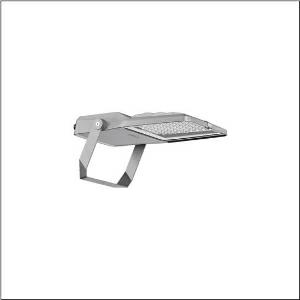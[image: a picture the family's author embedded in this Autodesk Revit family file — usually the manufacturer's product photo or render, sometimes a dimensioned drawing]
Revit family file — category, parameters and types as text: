
# Revit family: floodlight_fl_21_iq_mini___pl43_5xa7772c5a1a_be68
name_source: partatom
category: Lighting Fixtures
units: mm (PartAtom-declared; Revit-internal decimal feet)

## family parameters
Cut with Voids When Loaded = No
Host = Face
Light Source = No
Part Type = Normal
Room Calculation Point = No
Round Connector Dimension = Use Diameter
Shared = No

## types (1)
- --- (1 x LED, 11690 lm, 87.2 W, 4000K)
    Apparent Load = 87 VA
    CIE Flux Codes = 27 78 99 100 100
    Color Rendering = 80
    Color Temperature = 4000K
    Default Elevation = 1800 mm
    Description = Floodlight FL 21 iQ mini, floodlight, primary light control with lens, of PMMA, primary optical cover: protective disc, of toughened safety glass, transparent, light distribution: PL43, light emission: direct distribution, installation type: surface-mounted, lamps: LED, High Power LED, rated values: 11.690lm | 87,2W | 134,1lm/W (begin service life); end service life: 11.690lm | 92,1W; at 50% lumin. flux: 5.845lm | 40,1W | 145,8lm/W, colour temperature: 4000K, colour rendering: CRI > 80, light colour: 840, light setting 1 begin service life: 100% | 11.690lm | 87,2W | 134,1lm/W | 4.000K, light setting 1 end service life: 92,1W, further light settings possible, control: Street-Remote, Auto-Match, Temp-Guard, Night-Set, Smart-Wire, Desk-Remote (wireless, voltage-free reading and setting of iQ features in the workshop via application-optimized NFC function/RFID function), optimised constant luminous flux control (CLO 2.0), pre-setting: linear dimming characteristic, with terminal, 6-pole, mains connection: 220..240V, AC, 50/60Hz, luminaire housing, of diecast aluminium, powder-coated, SITECO metallic grey (DB 702S), corrosivity category C5 mid according to DIN EN ISO 12944suitable for swimming poolschlorine-resistant, sealing non-destructively replaceable, mounting bracket, of steel, galvanised, powder-coated, SITECO metallic grey (DB 702S), protection rating (complete): IP66, insulation class (complete): insulation class II (safety insulation), certification: CE, ENEC, VDE, protection symbol: D, impact resistance: IK08, permissible operating ambient temperature: -40..+40°C, permissible operating ambient temperature for outdoor applications: -40..+50°C, standard: DIN EN 12944, LABS conformity tested according to VDMA 24364:2018-05, packaging unit: 1 piece

Light Distribution: PL43
    Height = 70 mm
    Lamp = 1 x LED
    Lamp Light Flux = 11690 lm
    Lamp Power = 87.2 W
    Lamp count = 1
    Length = 485 mm
    Luminous efficacy = 134 lm/W
    Manufacturer = Siteco
    ModVariant = No
    Model = 5XA7772C5A1A
    Number of Poles = 1
    OnlyDefault = Yes
    Power Factor = 1
    Product Name = Floodlight FL 21 iQ mini | PL43
    Product group = floodlight | pylon annexe
    ProductGroupID = 6201
    Protection Class = Protection class II
    Protection Degree = IP 66
    RLX_Detail_Level = 1
    RLX_Emergency_Light_Flux = 0 lm
    RLX_Emergency_Type = 0
    RLX_Emergency_Type_DB = No
    RlxData = <blob elided: 96501 chars, md5=ec8fbeb1>
    Socket = socket
    Standby Power = 0 W
    System Light Flux = 11690 lm
    System Power = 87 W
    Type Comments = factory setting: luminous flux: 100 % | dim-lin: 254 | 456 mA
    Type Image = l_1006845.jpg
    URL = http://relux.com
    VarID = @adj_161587
    Voltage = 0 V
    Weight = 0.00 kg
    Width = 337 mm

## geometry (parser evidence)
native form markers: Blend x4, Sweep x14
no freeform markers — native parametric forms only
